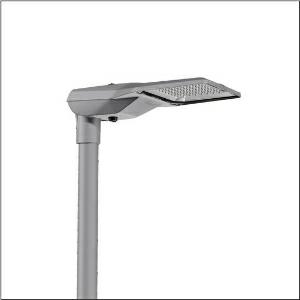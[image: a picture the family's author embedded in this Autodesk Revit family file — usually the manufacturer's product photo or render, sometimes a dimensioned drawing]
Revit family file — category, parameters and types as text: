
# Revit family: streetlight_sl_21_midi___st1_0a_5xe3d63t08nb_4f09
name_source: partatom
category: Lighting Fixtures
units: mm (PartAtom-declared; Revit-internal decimal feet)

## family parameters
Cut with Voids When Loaded = No
Host = Face
Light Source = No
Part Type = Normal
Room Calculation Point = No
Round Connector Dimension = Use Diameter
Shared = No

## types (1)
- --- (1 x LED, 20350 lm, 151.2 W, 2700K)
    Apparent Load = 151 VA
    CIE Flux Codes = 40 73 97 100 100
    Color Rendering = 70
    Color Temperature = 2700K
    Default Elevation = 1800 mm
    Description = Streetlight SL 21 midi, mast luminaire, primary light control with lens, of PMMA, primary optical cover: cover, of toughened safety glass, transparent, light distribution: ST1.0a, light emission: direct distribution, primary light characteristic: asymmetric, installation type: side-entry, post-top, LED, High Power LED, rated luminous flux: 20.350lm, luminous efficacy: 135lm/W, light colour: 727, colour temperature: 2700K, control gear: D4i, control: overheat protection, constant luminous flux control, time-dependent luminous flux control, flexible luminous flux parameterisation, pre-setting: logarithmic dimming characteristic, mains connection: 230..240V, AC, 50/60Hz, start of lifetime: 151W, end of service life: 157W, reduction: 70W, luminaire housing, of diecast aluminium, powder-coated, Siteco® metallic grey (DB 702S), corrosivity category C5 mid according to DIN EN ISO 12944, please order mast flange separately, inclination adjustable: 0°, 5°, 10°, 15°, sealing non-destructively replaceable, multi-level sealing system, length: 644mm, width: 335mm, height: 110mm, mast flange for spigot size: 42mm (side-entry): 5XC10008XM4, 60/48mm (side-entry/post-top): 5XC10108XM2, 76/60mm (side-entry/post-top): 5XC10108XM1, mounting height: 4..8m, Smart Interface below and above, protection rating (complete): IP66, insulation class (complete): insulation class II (safety insulation), certification: CE, ENEC, ENEC+, VDE, impact resistance: IK10, permissible operating ambient temperature for outdoor applications: -40..+50°C, standard-compliant lighting for roads and squares, packaging unit: 1 piece

Light Distribution: ST1.0a
    Height = 111 mm
    Lamp = 1 x LED
    Lamp Light Flux = 20350 lm
    Lamp Power = 151.2 W
    Lamp count = 1
    Length = 644 mm
    Luminous efficacy = 135 lm/W
    Manufacturer = Siteco
    ModVariant = No
    Model = 5XE3D63T08NB
    Number of Poles = 1
    OnlyDefault = Yes
    Power Factor = 1
    Product Name = Streetlight SL 21 midi | ST1.0a
    Product group = mast luminaire | pylon top
    ProductGroupID = 6100
    Protection Class = Protection class II
    Protection Degree = IP 66
    RLX_Detail_Level = 1
    RLX_Emergency_Light_Flux = 0 lm
    RLX_Emergency_Type = 0
    RLX_Emergency_Type_DB = No
    RlxData = <blob elided: 27133 chars, md5=fc67f92e>
    Socket = socket
    Standby Power = 0 W
    System Light Flux = 20350 lm
    System Power = 151 W
    Type Comments = factory setting: luminous flux: 100 % | dim-lin: 254 | 802 mA
    Type Image = l_1004304.jpg
    URL = http://relux.com
    VarID = @adj_170424
    Voltage = 0 V
    Weight = 0.00 kg
    Width = 336 mm

## geometry (parser evidence)
native form markers: Blend x4, Sweep x11
no freeform markers — native parametric forms only
